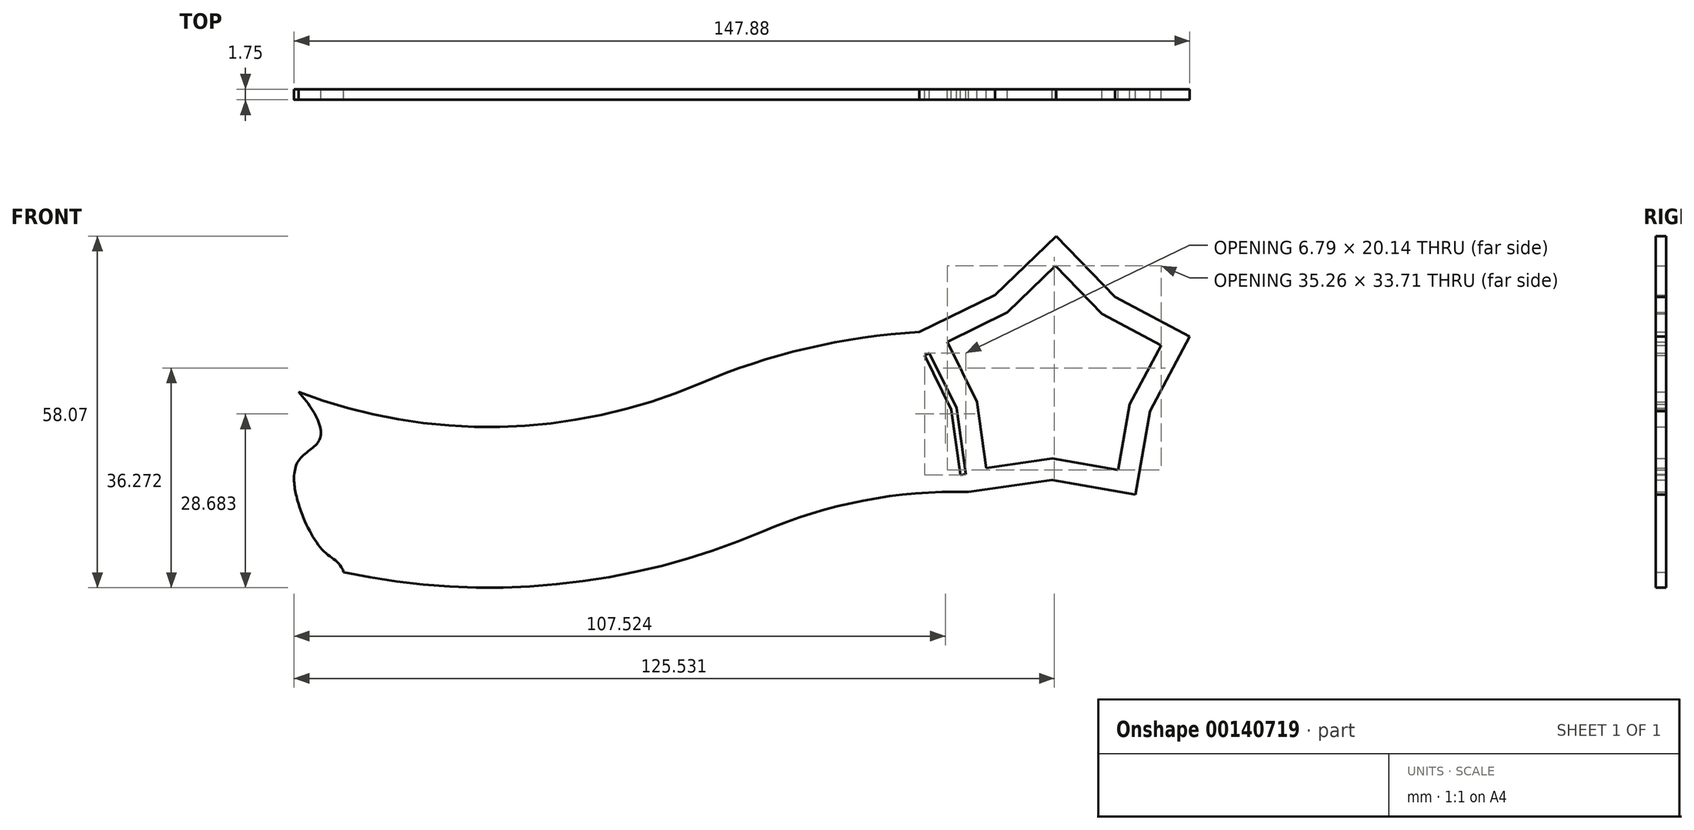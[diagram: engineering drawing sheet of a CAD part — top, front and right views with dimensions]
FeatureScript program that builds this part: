
annotation { "Feature Type Name" : "Feature", "Feature Type Description" : "" }
export const myFeature = defineFeature(function(context is Context, id is Id, definition is map)
    precondition{}
    {
        {
            var Q0;
            Q0=qCreatedBy(makeId("Front.planeOp"),FACE);
            var sketch = newSketch(context, id + "F0", { "sketchPlane" : qUnion([Q0])});
            skLineSegment(sketch, "E0", {"start": v(65.49, 43.12) * mm, "end": v(83.74, 60.8) * mm});
            skLineSegment(sketch, "E1", {"start": v(83.74, 60.8) * mm, "end": v(101.41, 42.54) * mm});
            skLineSegment(sketch, "E2.1.0", {"start": v(53.83, 9.13) * mm, "end": v(42.67, 31.95) * mm});
            skLineSegment(sketch, "E2.1.1", {"start": v(42.67, 31.95) * mm, "end": v(65.49, 43.12) * mm});
            skLineSegment(sketch, "E2.2.0", {"start": v(82.56, -12.45) * mm, "end": v(57.4, -16.02) * mm});
            skLineSegment(sketch, "E2.2.1", {"start": v(57.4, -16.02) * mm, "end": v(53.83, 9.13) * mm});
            skPoint(sketch, "E2.center", {"position": v(83.87, 15.76) * mm});
            skLineSegment(sketch, "E3.1.3.0", {"start": v(111.97, 8.2) * mm, "end": v(107.59, -16.83) * mm});
            skLineSegment(sketch, "E3.3.3.0", {"start": v(107.59, -16.83) * mm, "end": v(82.56, -12.45) * mm});
            skLineSegment(sketch, "E3.1.4.0", {"start": v(101.41, 42.54) * mm, "end": v(123.86, 30.65) * mm});
            skLineSegment(sketch, "E3.3.4.0", {"start": v(123.86, 30.65) * mm, "end": v(111.97, 8.2) * mm});
            skPoint(sketch, "E4.3.internal.snap0", {"position": v(55.84, -5) * mm});
            skArc(sketch, "E5", {"start": v(42.67, 31.95) * mm, "mid": v(8.98, 27.07) * mm, "end": v(-23.36, 16.43) * mm});
            skArc(sketch, "E6", {"start": v(-143.62, 13.97) * mm, "mid": v(-83.25, 3.5) * mm, "end": v(-23.36, 16.43) * mm});
            skArc(sketch, "E7.0", {"start": v(48.45, 20.13) * mm, "mid": v(14.22, 15.9) * mm, "end": v(-18.61, 5.35) * mm});
            skArc(sketch, "E7.1", {"start": v(-137.63, -0.85) * mm, "mid": v(-77.57, -8.36) * mm, "end": v(-18.61, 5.35) * mm});
            skArc(sketch, "E8.0", {"start": v(53.97, 8.14) * mm, "mid": v(19.35, 4.65) * mm, "end": v(-13.86, -5.74) * mm});
            skArc(sketch, "E8.1", {"start": v(-145, -11.15) * mm, "mid": v(-78.93, -20.5) * mm, "end": v(-13.86, -5.74) * mm});
            skArc(sketch, "E9.0", {"start": v(55.69, -3.93) * mm, "mid": v(22.61, -7) * mm, "end": v(-9.11, -16.83) * mm});
            skArc(sketch, "E9.1", {"start": v(-141.76, -24.8) * mm, "mid": v(-74.74, -32.36) * mm, "end": v(-9.11, -16.83) * mm});
            skArc(sketch, "E10.0", {"start": v(-130.14, -40.17) * mm, "mid": v(-66.3, -43.8) * mm, "end": v(-4.36, -27.92) * mm});
            skArc(sketch, "E10.1", {"start": v(57.4, -16.02) * mm, "mid": v(25.88, -18.64) * mm, "end": v(-4.36, -27.92) * mm});
            skFitSpline(sketch, "E11", {"points": [v(-143.62, 13.97) * mm, v(-137.22, 0) * mm, v(-143.62, -6.6) * mm, v(-143.62, -19.8) * mm, v(-135.75, -34.14) * mm, v(-130.14, -40.17) * mm], "startDerivative": vector(56.82, -63.91) * mm, "endDerivative": vector(19.2, -59.24) * mm});
            skLineSegment(sketch, "E12", {"start": v(57.4, -16.02) * mm, "end": v(123.86, 30.65) * mm, "construction": true});
            skLineSegment(sketch, "E13", {"start": v(57.4, -16.02) * mm, "end": v(83.74, 60.8) * mm, "construction": true});
            skLineSegment(sketch, "E14", {"start": v(107.59, -16.83) * mm, "end": v(42.67, 31.95) * mm, "construction": true});
            skLineSegment(sketch, "E15", {"start": v(123.86, 30.65) * mm, "end": v(42.67, 31.95) * mm, "construction": true});
            skLineSegment(sketch, "E16", {"start": v(107.59, -16.83) * mm, "end": v(83.74, 60.8) * mm, "construction": true});
            skLineSegment(sketch, "E17", {"start": v(-23.36, 16.43) * mm, "end": v(-18.61, 5.35) * mm, "construction": true});
            skLineSegment(sketch, "E18", {"start": v(-18.61, 5.35) * mm, "end": v(-13.86, -5.74) * mm, "construction": true});
            skLineSegment(sketch, "E19", {"start": v(-13.86, -5.74) * mm, "end": v(-9.11, -16.83) * mm, "construction": true});
            skLineSegment(sketch, "E20", {"start": v(-9.11, -16.83) * mm, "end": v(-4.36, -27.92) * mm, "construction": true});
            skLineSegment(sketch, "E21.0", {"start": v(59.98, 11.02) * mm, "end": v(51.16, 29.04) * mm});
            skLineSegment(sketch, "E21.1", {"start": v(62.8, -8.85) * mm, "end": v(59.98, 11.02) * mm});
            skLineSegment(sketch, "E21.2", {"start": v(51.16, 29.04) * mm, "end": v(69.18, 37.86) * mm});
            skLineSegment(sketch, "E21.3", {"start": v(82.66, -6.03) * mm, "end": v(62.8, -8.85) * mm});
            skLineSegment(sketch, "E21.4", {"start": v(102.43, -9.48) * mm, "end": v(82.66, -6.03) * mm});
            skLineSegment(sketch, "E21.5", {"start": v(105.88, 10.28) * mm, "end": v(102.43, -9.48) * mm});
            skLineSegment(sketch, "E21.6", {"start": v(69.18, 37.86) * mm, "end": v(83.6, 51.82) * mm});
            skLineSegment(sketch, "E21.7", {"start": v(83.6, 51.82) * mm, "end": v(97.55, 37.4) * mm});
            skLineSegment(sketch, "E21.8", {"start": v(97.55, 37.4) * mm, "end": v(115.28, 28) * mm});
            skLineSegment(sketch, "E21.9", {"start": v(115.28, 28) * mm, "end": v(105.88, 10.28) * mm});
            skLineSegment(sketch, "E22.0", {"start": v(72.27, 14.8) * mm, "end": v(68.15, 23.21) * mm});
            skLineSegment(sketch, "E22.1", {"start": v(73.59, 5.51) * mm, "end": v(72.27, 14.8) * mm});
            skLineSegment(sketch, "E22.2", {"start": v(68.15, 23.21) * mm, "end": v(76.57, 27.34) * mm});
            skLineSegment(sketch, "E22.3", {"start": v(82.87, 6.83) * mm, "end": v(73.59, 5.51) * mm});
            skLineSegment(sketch, "E22.4", {"start": v(92.1, 5.22) * mm, "end": v(82.87, 6.83) * mm});
            skLineSegment(sketch, "E22.5", {"start": v(93.72, 14.45) * mm, "end": v(92.1, 5.22) * mm});
            skLineSegment(sketch, "E22.6", {"start": v(76.57, 27.34) * mm, "end": v(83.3, 33.86) * mm});
            skLineSegment(sketch, "E22.7", {"start": v(83.3, 33.86) * mm, "end": v(89.83, 27.12) * mm});
            skLineSegment(sketch, "E22.8", {"start": v(89.83, 27.12) * mm, "end": v(98.11, 22.73) * mm});
            skLineSegment(sketch, "E22.9", {"start": v(98.11, 22.73) * mm, "end": v(93.72, 14.45) * mm});
            skSolve(sketch);
        }
        {
            var Q0;
            Q0 = qSketchRegion(id + "F0", true);
            extrude(context, id + "F1", {"entities" : qUnion([Q0]), "depth" : 3.17 * mm});
        }
        {
            var Q0;
            Q0=qCreatedBy(makeId("Front.planeOp"),FACE);
            var sketch = newSketch(context, id + "F2", { "sketchPlane" : qUnion([Q0])});
            skLineSegment(sketch, "E23.0", {"start": v(53.83, 9.13) * mm, "end": v(45.73, 25.68) * mm});
            skLineSegment(sketch, "E23.1", {"start": v(56.65, -10.72) * mm, "end": v(53.83, 9.13) * mm});
            skLineSegment(sketch, "E24.0", {"start": v(52.3, 8.66) * mm, "end": v(44.3, 24.98) * mm});
            skLineSegment(sketch, "E24.1", {"start": v(55.08, -10.94) * mm, "end": v(52.3, 8.66) * mm});
            skLineSegment(sketch, "E25", {"start": v(44.3, 24.98) * mm, "end": v(45.73, 25.68) * mm});
            skLineSegment(sketch, "E26", {"start": v(55.08, -10.94) * mm, "end": v(56.65, -10.72) * mm});
            skPoint(sketch, "E27.orphan", {"position": v(42.67, 31.95) * mm});
            skPoint(sketch, "E28.orphan", {"position": v(57.4, -16.02) * mm});
            skCircle(sketch, "E29", {"center": v(-124.86, -4.28) * mm, "radius": 0.95 * mm});
            skCircle(sketch, "E30.1.0.0", {"center": v(-121.06, -3.94) * mm, "radius": 0.95 * mm});
            skCircle(sketch, "E30.2.0.0", {"center": v(-117.27, -3.6) * mm, "radius": 0.95 * mm});
            skCircle(sketch, "E30.3.0.0", {"center": v(-113.47, -3.25) * mm, "radius": 0.95 * mm});
            skCircle(sketch, "E30.4.0.0", {"center": v(-109.68, -2.9) * mm, "radius": 0.95 * mm});
            skCircle(sketch, "E30.5.0.0", {"center": v(-105.88, -2.56) * mm, "radius": 0.95 * mm});
            skCircle(sketch, "E30.6.0.0", {"center": v(-102.09, -2.22) * mm, "radius": 0.95 * mm});
            skCircle(sketch, "E30.7.0.0", {"center": v(-98.3, -1.88) * mm, "radius": 0.95 * mm});
            skCircle(sketch, "E30.8.0.0", {"center": v(-94.5, -1.53) * mm, "radius": 0.95 * mm});
            skCircle(sketch, "E30.9.0.0", {"center": v(-90.7, -1.19) * mm, "radius": 0.95 * mm});
            skCircle(sketch, "E30.10.0.0", {"center": v(-86.91, -0.84) * mm, "radius": 0.95 * mm});
            skCircle(sketch, "E30.11.0.0", {"center": v(-83.12, -0.5) * mm, "radius": 0.95 * mm});
            skCircle(sketch, "E30.12.0.0", {"center": v(-79.32, -0.16) * mm, "radius": 0.95 * mm});
            skCircle(sketch, "E30.13.0.0", {"center": v(-75.53, 0.19) * mm, "radius": 0.95 * mm});
            skCircle(sketch, "E30.14.0.0", {"center": v(-71.73, 0.53) * mm, "radius": 0.95 * mm});
            skCircle(sketch, "E30.15.0.0", {"center": v(-67.94, 0.88) * mm, "radius": 0.95 * mm});
            skCircle(sketch, "E30.16.0.0", {"center": v(-64.15, 1.22) * mm, "radius": 0.95 * mm});
            skCircle(sketch, "E30.17.0.0", {"center": v(-60.35, 1.56) * mm, "radius": 0.95 * mm});
            skCircle(sketch, "E30.18.0.0", {"center": v(-56.56, 1.9) * mm, "radius": 0.95 * mm});
            skCircle(sketch, "E30.19.0.0", {"center": v(-52.76, 2.25) * mm, "radius": 0.95 * mm});
            skCircle(sketch, "E30.20.0.0", {"center": v(-48.97, 2.6) * mm, "radius": 0.95 * mm});
            skCircle(sketch, "E30.21.0.0", {"center": v(-45.17, 2.94) * mm, "radius": 0.95 * mm});
            skCircle(sketch, "E30.22.0.0", {"center": v(-41.38, 3.28) * mm, "radius": 0.95 * mm});
            skCircle(sketch, "E30.23.0.0", {"center": v(-37.58, 3.63) * mm, "radius": 0.95 * mm});
            skCircle(sketch, "E30.24.0.0", {"center": v(-33.79, 3.97) * mm, "radius": 0.95 * mm});
            skCircle(sketch, "E30.25.0.0", {"center": v(-30, 4.31) * mm, "radius": 0.95 * mm});
            skCircle(sketch, "E30.26.0.0", {"center": v(-26.2, 4.66) * mm, "radius": 0.95 * mm});
            skCircle(sketch, "E30.27.0.0", {"center": v(-22.4, 5) * mm, "radius": 0.95 * mm});
            skCircle(sketch, "E30.28.0.0", {"center": v(-18.61, 5.35) * mm, "radius": 0.95 * mm});
            skLineSegment(sketch, "E30.direction1", {"start": v(-124.86, -4.28) * mm, "end": v(-121.06, -3.94) * mm, "construction": true});
            skCircle(sketch, "E31.2.0.0", {"center": v(-123.8, -16.86) * mm, "radius": 0.95 * mm});
            skCircle(sketch, "E32.1.0.0", {"center": v(-120, -16.47) * mm, "radius": 0.95 * mm});
            skCircle(sketch, "E32.2.0.0", {"center": v(-116.2, -16.09) * mm, "radius": 0.95 * mm});
            skLineSegment(sketch, "E32.direction1", {"start": v(-123.8, -16.86) * mm, "end": v(-120, -16.47) * mm, "construction": true});
            skCircle(sketch, "E33.0.3.0", {"center": v(-112.42, -15.7) * mm, "radius": 0.95 * mm});
            skCircle(sketch, "E33.0.4.0", {"center": v(-108.63, -15.32) * mm, "radius": 0.95 * mm});
            skCircle(sketch, "E33.0.5.0", {"center": v(-104.84, -14.94) * mm, "radius": 0.95 * mm});
            skCircle(sketch, "E33.0.6.0", {"center": v(-101.05, -14.56) * mm, "radius": 0.95 * mm});
            skCircle(sketch, "E33.0.7.0", {"center": v(-97.26, -14.17) * mm, "radius": 0.95 * mm});
            skCircle(sketch, "E33.0.8.0", {"center": v(-93.47, -13.79) * mm, "radius": 0.95 * mm});
            skCircle(sketch, "E33.0.9.0", {"center": v(-89.68, -13.4) * mm, "radius": 0.95 * mm});
            skCircle(sketch, "E33.0.10.0", {"center": v(-85.88, -13.02) * mm, "radius": 0.95 * mm});
            skCircle(sketch, "E33.0.11.0", {"center": v(-82.1, -12.64) * mm, "radius": 0.95 * mm});
            skCircle(sketch, "E33.0.12.0", {"center": v(-78.3, -12.26) * mm, "radius": 0.95 * mm});
            skCircle(sketch, "E33.0.13.0", {"center": v(-74.51, -11.87) * mm, "radius": 0.95 * mm});
            skCircle(sketch, "E33.0.14.0", {"center": v(-70.72, -11.5) * mm, "radius": 0.95 * mm});
            skCircle(sketch, "E33.0.15.0", {"center": v(-66.93, -11.1) * mm, "radius": 0.95 * mm});
            skCircle(sketch, "E33.0.16.0", {"center": v(-63.14, -10.72) * mm, "radius": 0.95 * mm});
            skCircle(sketch, "E33.0.17.0", {"center": v(-59.35, -10.34) * mm, "radius": 0.95 * mm});
            skCircle(sketch, "E33.0.18.0", {"center": v(-55.56, -9.96) * mm, "radius": 0.95 * mm});
            skCircle(sketch, "E33.0.19.0", {"center": v(-51.77, -9.57) * mm, "radius": 0.95 * mm});
            skCircle(sketch, "E34.0.20.0", {"center": v(-47.98, -9.2) * mm, "radius": 0.95 * mm});
            skCircle(sketch, "E34.0.21.0", {"center": v(-44.19, -8.8) * mm, "radius": 0.95 * mm});
            skCircle(sketch, "E34.0.22.0", {"center": v(-40.4, -8.42) * mm, "radius": 0.95 * mm});
            skCircle(sketch, "E34.0.23.0", {"center": v(-36.6, -8.04) * mm, "radius": 0.95 * mm});
            skCircle(sketch, "E34.0.24.0", {"center": v(-32.82, -7.66) * mm, "radius": 0.95 * mm});
            skCircle(sketch, "E34.0.25.0", {"center": v(-29.02, -7.27) * mm, "radius": 0.95 * mm});
            skCircle(sketch, "E34.0.26.0", {"center": v(-25.23, -6.9) * mm, "radius": 0.95 * mm});
            skCircle(sketch, "E34.0.27.0", {"center": v(-21.44, -6.5) * mm, "radius": 0.95 * mm});
            skCircle(sketch, "E34.0.28.0", {"center": v(-17.65, -6.12) * mm, "radius": 0.95 * mm});
            skCircle(sketch, "E34.0.29.0", {"center": v(-13.86, -5.74) * mm, "radius": 0.95 * mm});
            skCircle(sketch, "E35.0.30.0", {"center": v(-10.07, -5.36) * mm, "radius": 0.95 * mm});
            skCircle(sketch, "E36.0.31.0", {"center": v(-6.28, -4.98) * mm, "radius": 0.95 * mm});
            skCircle(sketch, "E36.0.32.0", {"center": v(-2.49, -4.6) * mm, "radius": 0.95 * mm});
            skSolve(sketch);
        }
        {
            var Q0;
            Q0=makeQuery(id+"F2.imprint","IMPRINT",FACE,{"disambiguationData":[TD([[makeQuery(id+"F2.imprint","IMPRINT",EDGE,{"derivedFrom":sQuery(id+"F2.wireOp",EDGE,"E23.0")}),1.0]])]});
            extrude(context, id + "F3", {"entities" : qUnion([Q0]), "operationType" : NewBodyOperationType.REMOVE, "depth" : 25.4 * mm});
        }
        {
            var Q0;
            Q0=makeQuery(id+"F1.opExtrude","SWEPT_BODY",BODY,{"disambiguationData":[OSD([sQuery(id+"F0.wireOp",EDGE,"E0"),sQuery(id+"F0.wireOp",EDGE,"E1"),sQuery(id+"F0.wireOp",EDGE,"E2.1.1"),sQuery(id+"F0.wireOp",EDGE,"E2.2.0"),sQuery(id+"F0.wireOp",EDGE,"E3.1.3.0"),sQuery(id+"F0.wireOp",EDGE,"E3.3.3.0"),sQuery(id+"F0.wireOp",EDGE,"E3.1.4.0"),sQuery(id+"F0.wireOp",EDGE,"E3.3.4.0"),sQuery(id+"F0.wireOp",EDGE,"E5"),sQuery(id+"F0.wireOp",EDGE,"E6"),sQuery(id+"F0.wireOp",EDGE,"E10.0"),sQuery(id+"F0.wireOp",EDGE,"E10.1"),sQuery(id+"F0.wireOp",EDGE,"E11")])]});
            var Q1;
            Q1=qCreatedBy(makeId("Origin.pointOp"),VERTEX);
            transform(context, id + "F4", {"entities" : qUnion([Q0]), "transformType" : TransformType.SCALE_UNIFORMLY, "scale" : .55, "scalePoint" : qUnion([Q1]), "makeCopy" : false});
        }
    });
